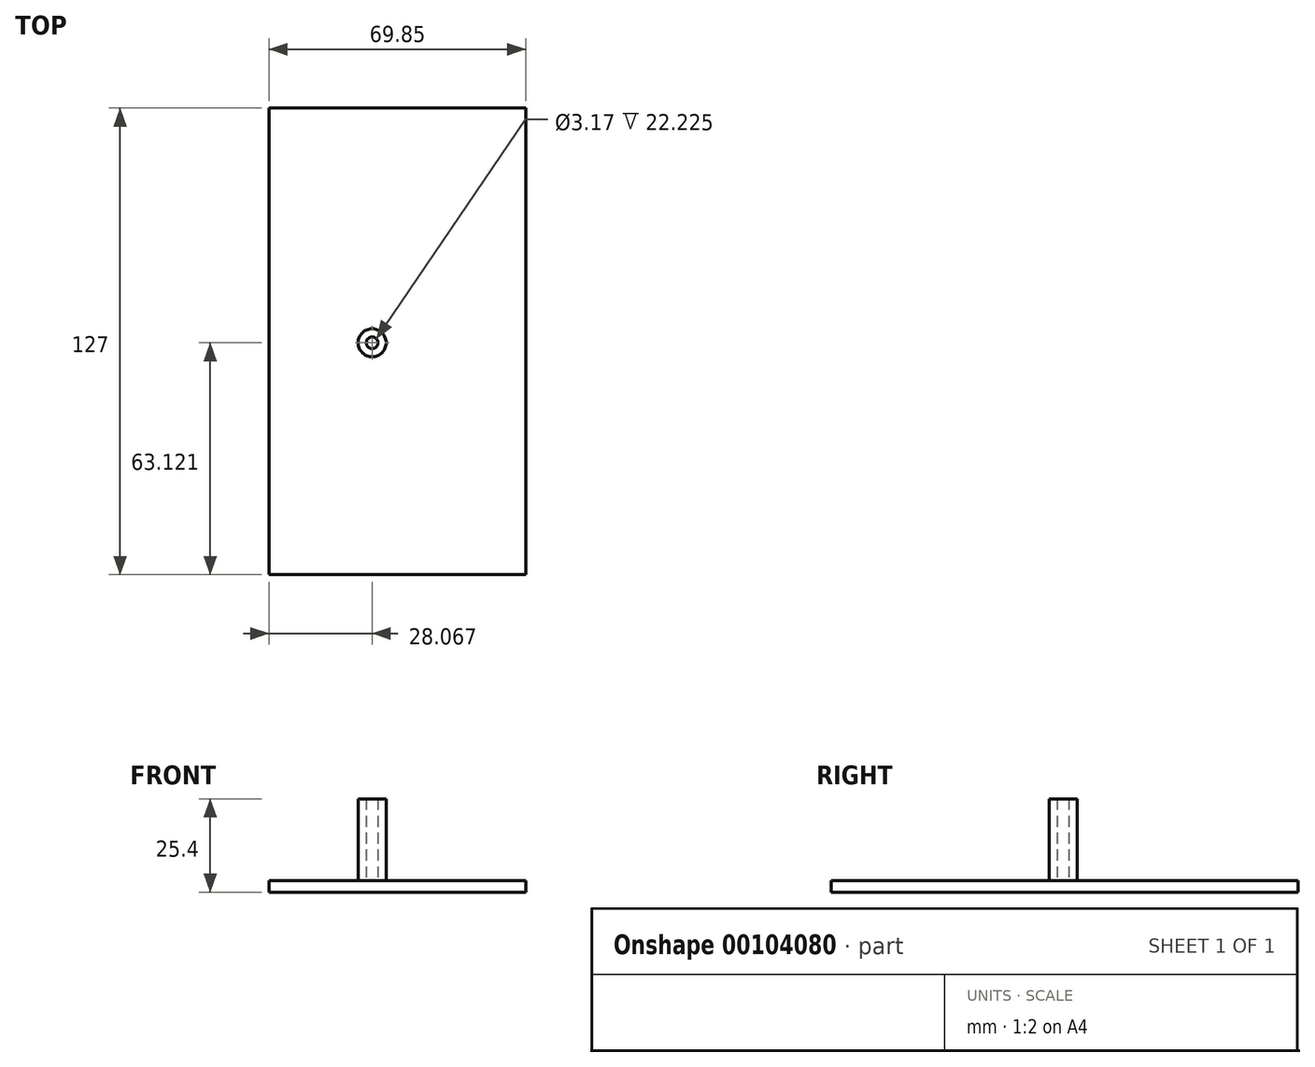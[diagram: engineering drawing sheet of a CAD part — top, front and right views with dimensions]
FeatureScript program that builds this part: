
annotation { "Feature Type Name" : "Feature", "Feature Type Description" : "" }
export const myFeature = defineFeature(function(context is Context, id is Id, definition is map)
    precondition{}
    {
        {
            var Q0;
            Q0=qCreatedBy(makeId("Top.planeOp"),FACE);
            var sketch = newSketch(context, id + "F0", { "sketchPlane" : qUnion([Q0])});
            skLineSegment(sketch, "E0.bottom", {"start": v(-47.27, -127.38) * mm, "end": v(22.58, -127.38) * mm});
            skLineSegment(sketch, "E0.top", {"start": v(-47.27, -0.38) * mm, "end": v(22.58, -0.38) * mm});
            skLineSegment(sketch, "E0.left", {"start": v(-47.27, -127.38) * mm, "end": v(-47.27, -0.38) * mm});
            skLineSegment(sketch, "E0.right", {"start": v(22.58, -127.38) * mm, "end": v(22.58, -0.38) * mm});
            skLineSegment(sketch, "E1", {"start": v(-47.27, -70.23) * mm, "end": v(22.58, -70.23) * mm});
            skPoint(sketch, "E2", {"position": v(-12.34, -70.23) * mm});
            skPoint(sketch, "E3", {"position": v(-5.9, -70.23) * mm});
            skPoint(sketch, "E4", {"position": v(-19.2, -70.23) * mm});
            skPoint(sketch, "E5", {"position": v(-19.2, -64.26) * mm});
            skCircle(sketch, "E6", {"center": v(-19.2, -64.26) * mm, "radius": 1.59 * mm});
            skCircle(sketch, "E7", {"center": v(-19.2, -64.26) * mm, "radius": 3.81 * mm});
            skSolve(sketch);
        }
        {
            var Q0;
            Q0 = qSketchRegion(id + "F0", true);
            var Q1;
            Q1=makeQuery(id+"F0.imprint","IMPRINT",FACE,{"disambiguationData":[TD([[makeQuery(id+"F0.imprint","IMPRINT",EDGE,{"derivedFrom":sQuery(id+"F0.wireOp",EDGE,"E6")}),1.0]])]});
            extrude(context, id + "F1", {"entities" : qUnion([Q0, Q1]), "depth" : 3.17 * mm});
        }
        {
            var Q0;
            Q0=makeQuery(id+"F0.imprint","IMPRINT",FACE,{"disambiguationData":[TD([[makeQuery(id+"F0.imprint","IMPRINT",EDGE,{"derivedFrom":sQuery(id+"F0.wireOp",EDGE,"E6")}),-1.0]])]});
            extrude(context, id + "F2", {"entities" : qUnion([Q0]), "operationType" : NewBodyOperationType.ADD, "depth" : 25.4 * mm});
        }
    });
